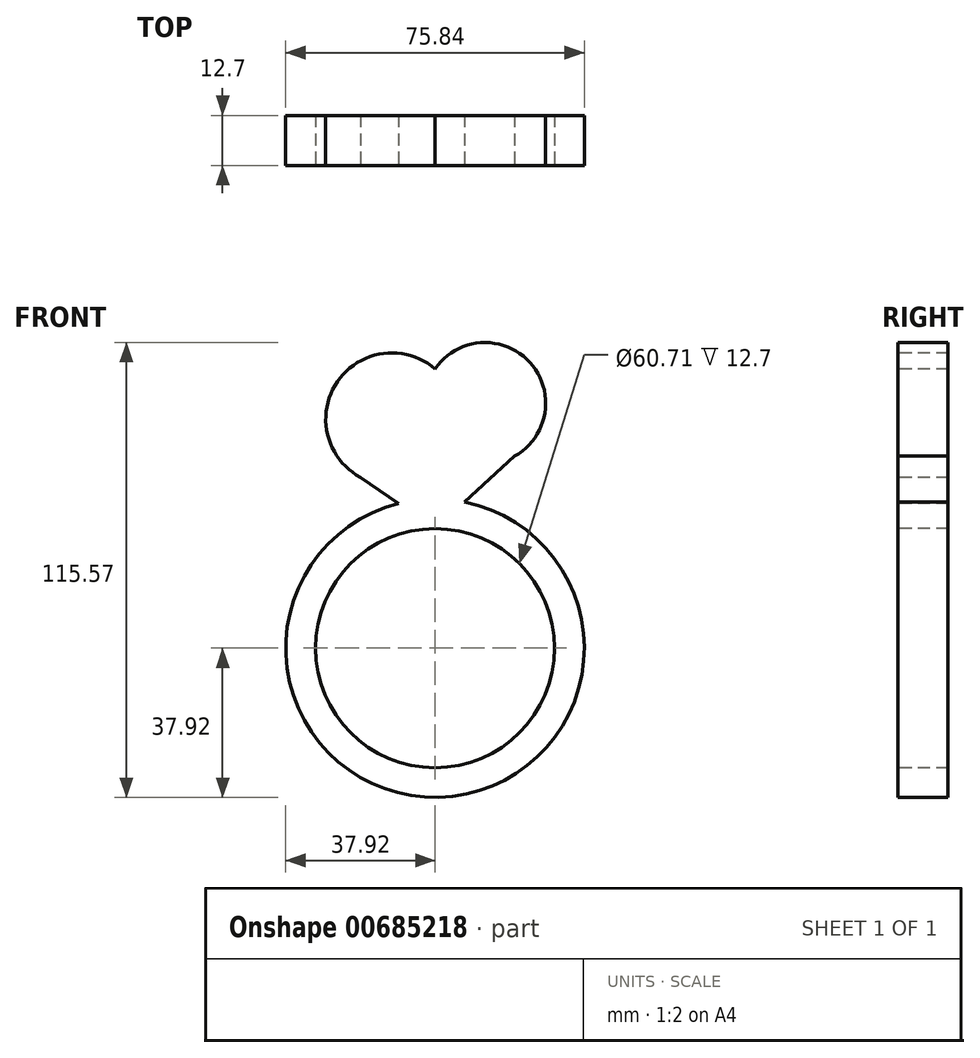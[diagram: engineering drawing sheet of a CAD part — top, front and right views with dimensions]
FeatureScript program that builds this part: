
annotation { "Feature Type Name" : "Feature", "Feature Type Description" : "" }
export const myFeature = defineFeature(function(context is Context, id is Id, definition is map)
    precondition{}
    {
        {
            var Q0;
            Q0=qCreatedBy(makeId("Front.planeOp"),FACE);
            var sketch = newSketch(context, id + "F0", { "sketchPlane" : qUnion([Q0])});
            skCircle(sketch, "E0", {"center": v(0, 0) * mm, "radius": 37.92 * mm});
            skCircle(sketch, "E1", {"center": v(0, 0) * mm, "radius": 30.36 * mm});
            skLineSegment(sketch, "E2", {"start": v(0, 30.36) * mm, "end": v(25.4, 53.49) * mm});
            skLineSegment(sketch, "E3", {"start": v(25.4, 53.49) * mm, "end": v(0, 70.97) * mm});
            skLineSegment(sketch, "E4", {"start": v(0, 30.36) * mm, "end": v(-21.87, 45.41) * mm});
            skLineSegment(sketch, "E5", {"start": v(-21.87, 45.41) * mm, "end": v(0, 70.97) * mm});
            skCircle(sketch, "E6", {"center": v(-10.94, 58.2) * mm, "radius": 16.82 * mm});
            skCircle(sketch, "E7", {"center": v(12.7, 62.23) * mm, "radius": 15.42 * mm});
            skSolve(sketch);
        }
        {
            var Q0;
            Q0 = qSketchRegion(id + "F0", true);
            extrude(context, id + "F1", {"entities" : qUnion([Q0]), "oppositeDirection" : true, "depth" : 12.7 * mm, "offsetDistance" : 25.4 * mm});
        }
        {
            var Q0;
            Q0 = qSketchRegion(id + "F0", true);
            var Q1;
            Q1=makeQuery(id+"F1.opExtrude","CAP_FACE",FACE,{"disambiguationData":[OSD([sQuery(id+"F0.wireOp",EDGE,"E0"),sQuery(id+"F0.wireOp",EDGE,"E1"),sQuery(id+"F0.wireOp",EDGE,"E2"),sQuery(id+"F0.wireOp",EDGE,"E4"),sQuery(id+"F0.wireOp",EDGE,"E6"),sQuery(id+"F0.wireOp",EDGE,"E7")])],"isStart":true});
            extrude(context, id + "F2", {"entities" : qUnion([Q0, Q1]), "operationType" : NewBodyOperationType.ADD, "oppositeDirection" : true, "depth" : 12.7 * mm, "offsetDistance" : 25.4 * mm});
        }
    });
